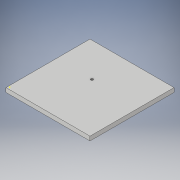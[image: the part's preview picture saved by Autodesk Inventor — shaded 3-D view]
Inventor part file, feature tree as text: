
AUTODESK INVENTOR PART (.ipt)
format: ipt  version: 2019 (Build 230136000, 136)  size: 96,768 bytes
history: native  units: mm
features: sketch x3, extrude x1, hole x1
ambient origin geometry x8: Origin, YZ Plane, XZ Plane, XY Plane, X Axis, Y Axis, Z Axis, Center Point
bodies: Solid1 (feature_tree)
feature tree (5):
  extrude  "Extrusion1"  Depth=600.0mm
  sketch  "Sketch2"  dims[d2=600.0mm d3=600.0mm]
  hole  "Hole1"  [1 undecoded]
  sketch  "Sketch1"  dims[d0=600.0mm d1=600.0mm]
  sketch  "Sketch3"  dims[d4=30.0mm d5=0.0mm d6=17.894mm d7=20.0mm d8=4.0mm d9=2.0mm d10=90.0deg d11=53.975mm d12=20.594885mm]
note: 1 required parameter value undecoded (feature->parameter linkage not recoverable at this tier; creation-order binding heuristic only, values carry confidence <= 0.55)
